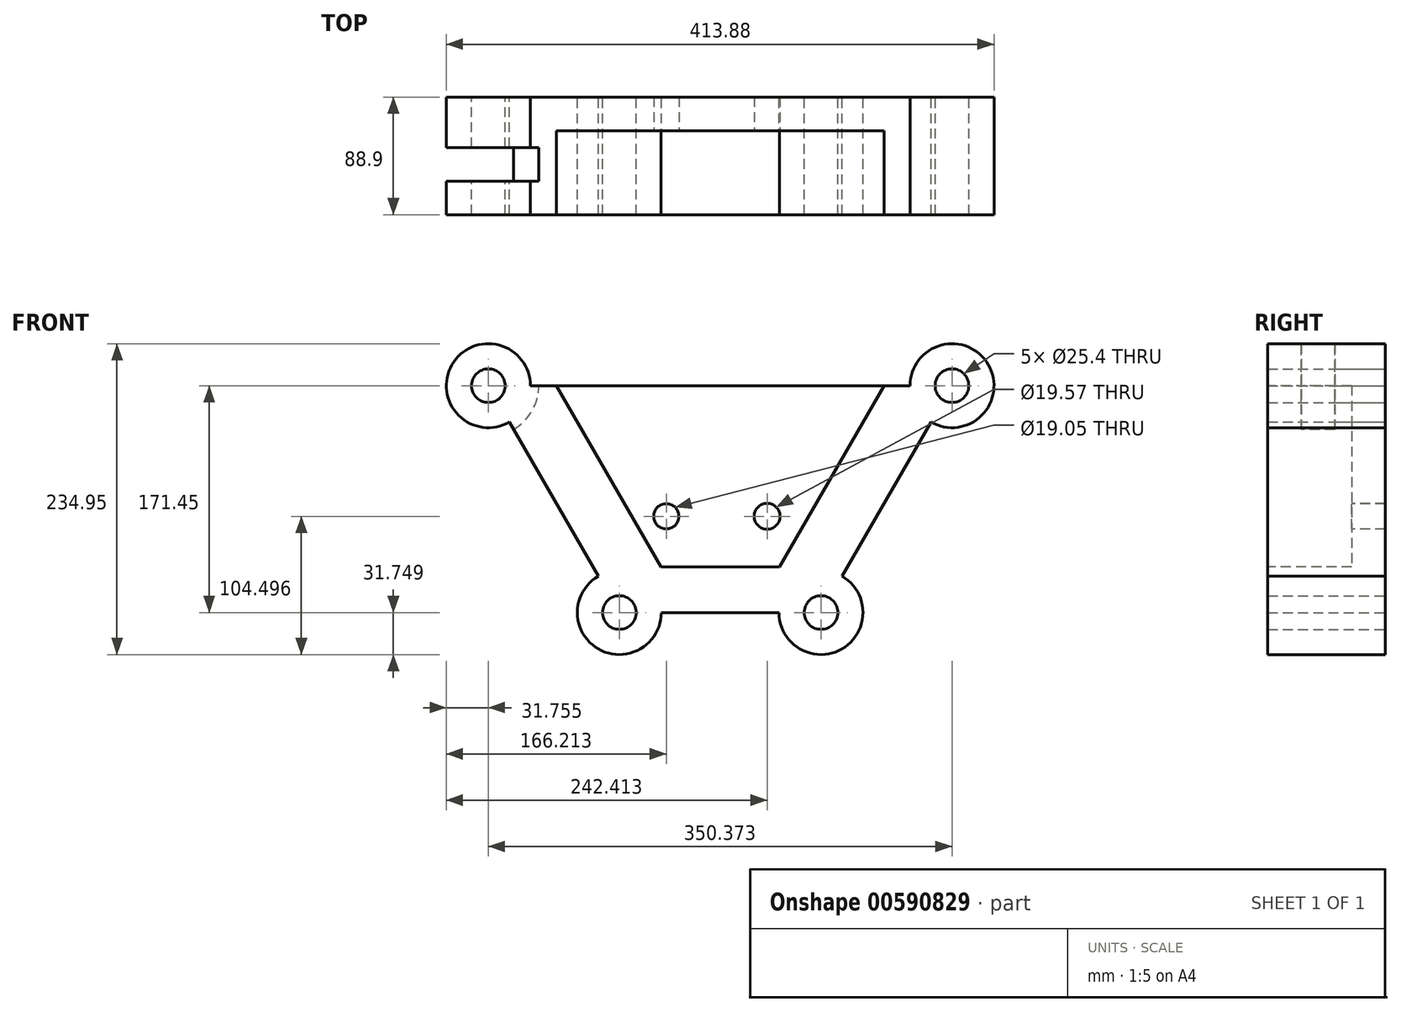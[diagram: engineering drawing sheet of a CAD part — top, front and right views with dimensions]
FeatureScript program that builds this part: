
annotation { "Feature Type Name" : "Feature", "Feature Type Description" : "" }
export const myFeature = defineFeature(function(context is Context, id is Id, definition is map)
    precondition{}
    {
        {
            var Q0;
            Q0=qCreatedBy(makeId("Front.planeOp"),FACE);
            var sketch = newSketch(context, id + "F0", { "sketchPlane" : qUnion([Q0])});
            skLineSegment(sketch, "E0", {"start": v(-63.64, -75.33) * mm, "end": v(88.76, -75.33) * mm});
            skLineSegment(sketch, "E1", {"start": v(-63.64, -75.33) * mm, "end": v(-162.63, 96.12) * mm});
            skLineSegment(sketch, "E2", {"start": v(-162.63, 96.12) * mm, "end": v(187.75, 96.12) * mm});
            skLineSegment(sketch, "E3", {"start": v(187.75, 96.12) * mm, "end": v(88.76, -75.33) * mm});
            skCircle(sketch, "E4", {"center": v(-63.64, -75.33) * mm, "radius": 12.7 * mm});
            skCircle(sketch, "E5", {"center": v(88.76, -75.33) * mm, "radius": 12.7 * mm});
            skCircle(sketch, "E6", {"center": v(-162.63, 96.12) * mm, "radius": 12.7 * mm});
            skCircle(sketch, "E7", {"center": v(187.75, 96.12) * mm, "radius": 12.7 * mm});
            skCircle(sketch, "E8", {"center": v(187.75, 96.12) * mm, "radius": 31.75 * mm});
            skCircle(sketch, "E9", {"center": v(88.76, -75.33) * mm, "radius": 31.75 * mm});
            skCircle(sketch, "E10", {"center": v(-63.64, -75.33) * mm, "radius": 31.75 * mm});
            skCircle(sketch, "E11", {"center": v(-162.63, 96.12) * mm, "radius": 31.75 * mm});
            skSolve(sketch);
        }
        {
            var Q0;
            {var subQ0=sQuery(id+"F0.wireOp",EDGE,"E11");var subQ1=sQuery(id+"F0.wireOp",EDGE,"E1");var subQ2=makeQuery(id+"F0.imprint","INTERSECT",VERTEX,{"derivedFrom":[subQ1,subQ0]});Q0=makeQuery(id+"F0.imprint","IMPRINT",FACE,{"disambiguationData":[TD([[makeQuery(id+"F0.imprint","IMPRINT",EDGE,{"disambiguationData":[TD([[subQ2,-1.0]])],"derivedFrom":subQ1}),1.0]])]});}
            var Q1;
            {var subQ0=sQuery(id+"F0.wireOp",EDGE,"E11");var subQ1=sQuery(id+"F0.wireOp",EDGE,"E1");var subQ2=makeQuery(id+"F0.imprint","INTERSECT",VERTEX,{"derivedFrom":[subQ1,subQ0]});Q1=makeQuery(id+"F0.imprint","IMPRINT",FACE,{"disambiguationData":[TD([[makeQuery(id+"F0.imprint","IMPRINT",EDGE,{"disambiguationData":[TD([[subQ2,-1.0]])],"derivedFrom":subQ1}),-1.0]])]});}
            var Q2;
            {var subQ0=sQuery(id+"F0.wireOp",EDGE,"E8");var subQ1=sQuery(id+"F0.wireOp",EDGE,"E2");var subQ2=makeQuery(id+"F0.imprint","INTERSECT",VERTEX,{"derivedFrom":[subQ1,subQ0]});Q2=makeQuery(id+"F0.imprint","IMPRINT",FACE,{"disambiguationData":[TD([[makeQuery(id+"F0.imprint","IMPRINT",EDGE,{"disambiguationData":[TD([[subQ2,-1.0]])],"derivedFrom":subQ1}),1.0]])]});}
            var Q3;
            {var subQ9=sQuery(id+"F0.wireOp",EDGE,"E10");var subQ13=sQuery(id+"F0.wireOp",EDGE,"E0");var subQ14=makeQuery(id+"F0.imprint","INTERSECT",VERTEX,{"derivedFrom":[subQ13,subQ9]});Q3=makeQuery(id+"F0.imprint","IMPRINT",FACE,{"disambiguationData":[TD([[makeQuery(id+"F0.imprint","IMPRINT",EDGE,{"disambiguationData":[TD([[subQ14,-1.0]])],"derivedFrom":subQ13}),1.0]])]});}
            var Q4;
            {var subQ0=sQuery(id+"F0.wireOp",EDGE,"E9");var subQ1=sQuery(id+"F0.wireOp",EDGE,"E0");var subQ2=makeQuery(id+"F0.imprint","INTERSECT",VERTEX,{"derivedFrom":[subQ1,subQ0]});Q4=makeQuery(id+"F0.imprint","IMPRINT",FACE,{"disambiguationData":[TD([[makeQuery(id+"F0.imprint","IMPRINT",EDGE,{"disambiguationData":[TD([[subQ2,-1.0]])],"derivedFrom":subQ1}),-1.0]])]});}
            var Q5;
            {var subQ0=sQuery(id+"F0.wireOp",EDGE,"E9");var subQ1=sQuery(id+"F0.wireOp",EDGE,"E0");var subQ2=makeQuery(id+"F0.imprint","INTERSECT",VERTEX,{"derivedFrom":[subQ1,subQ0]});Q5=makeQuery(id+"F0.imprint","IMPRINT",FACE,{"disambiguationData":[TD([[makeQuery(id+"F0.imprint","IMPRINT",EDGE,{"disambiguationData":[TD([[subQ2,-1.0]])],"derivedFrom":subQ1}),1.0]])]});}
            var Q6;
            {var subQ0=sQuery(id+"F0.wireOp",EDGE,"E10");var subQ1=sQuery(id+"F0.wireOp",EDGE,"E0");var subQ2=makeQuery(id+"F0.imprint","INTERSECT",VERTEX,{"derivedFrom":[subQ1,subQ0]});Q6=makeQuery(id+"F0.imprint","IMPRINT",FACE,{"disambiguationData":[TD([[makeQuery(id+"F0.imprint","IMPRINT",EDGE,{"disambiguationData":[TD([[subQ2,1.0]])],"derivedFrom":subQ1}),-1.0]])]});}
            var Q7;
            {var subQ0=sQuery(id+"F0.wireOp",EDGE,"E10");var subQ1=sQuery(id+"F0.wireOp",EDGE,"E0");var subQ2=makeQuery(id+"F0.imprint","INTERSECT",VERTEX,{"derivedFrom":[subQ1,subQ0]});Q7=makeQuery(id+"F0.imprint","IMPRINT",FACE,{"disambiguationData":[TD([[makeQuery(id+"F0.imprint","IMPRINT",EDGE,{"disambiguationData":[TD([[subQ2,1.0]])],"derivedFrom":subQ1}),1.0]])]});}
            var Q8;
            {var subQ0=sQuery(id+"F0.wireOp",EDGE,"E8");var subQ1=sQuery(id+"F0.wireOp",EDGE,"E2");var subQ2=makeQuery(id+"F0.imprint","INTERSECT",VERTEX,{"derivedFrom":[subQ1,subQ0]});Q8=makeQuery(id+"F0.imprint","IMPRINT",FACE,{"disambiguationData":[TD([[makeQuery(id+"F0.imprint","IMPRINT",EDGE,{"disambiguationData":[TD([[subQ2,-1.0]])],"derivedFrom":subQ1}),-1.0]])]});}
            extrude(context, id + "F1", {"entities" : qUnion([Q0, Q1, Q2, Q3, Q4, Q5, Q6, Q7, Q8]), "endBound" : BoundingType.SYMMETRIC, "depth" : 101.6 * mm, "offsetDistance" : 25.4 * mm});
        }
        {
            var Q0;
            Q0=makeQuery(id+"F1.opExtrude","CAP_FACE",FACE,{"disambiguationData":[OSD([sQuery(id+"F0.wireOp",EDGE,"E0"),sQuery(id+"F0.wireOp",EDGE,"E1"),sQuery(id+"F0.wireOp",EDGE,"E2"),sQuery(id+"F0.wireOp",EDGE,"E3"),sQuery(id+"F0.wireOp",EDGE,"E4"),sQuery(id+"F0.wireOp",EDGE,"E5"),sQuery(id+"F0.wireOp",EDGE,"E6"),sQuery(id+"F0.wireOp",EDGE,"E7"),sQuery(id+"F0.wireOp",EDGE,"E8"),sQuery(id+"F0.wireOp",EDGE,"E9"),sQuery(id+"F0.wireOp",EDGE,"E10"),sQuery(id+"F0.wireOp",EDGE,"E11")])],"isStart":false});
            var sketch = newSketch(context, id + "F2", { "sketchPlane" : qUnion([Q0])});
            skLineSegment(sketch, "E12", {"start": v(-111.3, 96.12) * mm, "end": v(-32.32, -40.68) * mm});
            skLineSegment(sketch, "E13", {"start": v(-32.32, -40.68) * mm, "end": v(57.44, -40.68) * mm});
            skLineSegment(sketch, "E14", {"start": v(57.44, -40.68) * mm, "end": v(136.42, 96.12) * mm});
            skLineSegment(sketch, "E15", {"start": v(136.42, 96.12) * mm, "end": v(-111.3, 96.12) * mm});
            skSolve(sketch);
        }
        {
            var Q0;
            Q0=makeQuery(id+"F2.imprint","IMPRINT",FACE,{"disambiguationData":[TD([[makeQuery(id+"F2.imprint","IMPRINT",EDGE,{"derivedFrom":sQuery(id+"F2.wireOp",EDGE,"E12")}),1.0]])]});
            extrude(context, id + "F3", {"entities" : qUnion([Q0]), "operationType" : NewBodyOperationType.REMOVE, "oppositeDirection" : true, "depth" : 76.2 * mm, "offsetDistance" : 25.4 * mm});
        }
        {
            var Q0;
            Q0=qCreatedBy(makeId("Front.planeOp"),FACE);
            var sketch = newSketch(context, id + "F4", { "sketchPlane" : qUnion([Q0])});
            skCircle(sketch, "E16", {"center": v(-162.63, 96.12) * mm, "radius": 38.1 * mm});
            skCircle(sketch, "E17", {"center": v(187.75, 96.12) * mm, "radius": 38.1 * mm});
            skCircle(sketch, "E18", {"center": v(-63.64, -75.33) * mm, "radius": 38.1 * mm});
            skCircle(sketch, "E19", {"center": v(88.76, -75.33) * mm, "radius": 38.1 * mm});
            skSolve(sketch);
        }
        {
            var Q0;
            Q0=makeQuery(id+"F4.imprint","IMPRINT",FACE,{"disambiguationData":[TD([[makeQuery(id+"F4.imprint","IMPRINT",EDGE,{"derivedFrom":sQuery(id+"F4.wireOp",EDGE,"E16")}),1.0]])]});
            var Q1;
            Q1=makeQuery(id+"F1.opExtrude","CAP_FACE",FACE,{"disambiguationData":[OSD([sQuery(id+"F0.wireOp",EDGE,"E0"),sQuery(id+"F0.wireOp",EDGE,"E1"),sQuery(id+"F0.wireOp",EDGE,"E2"),sQuery(id+"F0.wireOp",EDGE,"E3"),sQuery(id+"F0.wireOp",EDGE,"E4"),sQuery(id+"F0.wireOp",EDGE,"E5"),sQuery(id+"F0.wireOp",EDGE,"E6"),sQuery(id+"F0.wireOp",EDGE,"E7"),sQuery(id+"F0.wireOp",EDGE,"E8"),sQuery(id+"F0.wireOp",EDGE,"E9"),sQuery(id+"F0.wireOp",EDGE,"E10"),sQuery(id+"F0.wireOp",EDGE,"E11")])],"isStart":false});
            extrude(context, id + "F5", {"entities" : qUnion([Q0, Q1]), "operationType" : NewBodyOperationType.REMOVE, "endBound" : BoundingType.SYMMETRIC, "oppositeDirection" : true, "depth" : 25.4 * mm, "offsetDistance" : 25.4 * mm});
        }
        {
            var Q0;
            Q0=makeQuery(id+"F3.boolean.opBoolean","COPY",FACE,{"derivedFrom":makeQuery(id+"F3.opExtrude","CAP_FACE",FACE,{"disambiguationData":[OSD([sQuery(id+"F2.wireOp",EDGE,"E12"),sQuery(id+"F2.wireOp",EDGE,"E13"),sQuery(id+"F2.wireOp",EDGE,"E14"),sQuery(id+"F2.wireOp",EDGE,"E15")])],"isStart":false})});
            var sketch = newSketch(context, id + "F6", { "sketchPlane" : qUnion([Q0])});
            skCircle(sketch, "E20", {"center": v(-28.17, -2.58) * mm, "radius": 9.53 * mm});
            skCircle(sketch, "E21", {"center": v(48.03, -2.58) * mm, "radius": 9.78 * mm});
            skLineSegment(sketch, "E22", {"start": v(-28.17, -2.58) * mm, "end": v(48.03, -2.58) * mm, "construction": true});
            skPoint(sketch, "E23", {"position": v(9.93, 0) * mm});
            skLineSegment(sketch, "E24", {"start": v(9.93, 0) * mm, "end": v(9.93, -40.68) * mm, "construction": true});
            skPoint(sketch, "E24.endSnap0", {"position": v(12.56, -40.68) * mm});
            skLineSegment(sketch, "E25", {"start": v(9.93, -40.68) * mm, "end": v(12.56, -40.68) * mm, "construction": true});
            skSolve(sketch);
        }
        {
            var Q0;
            Q0=makeQuery(id+"F6.imprint","IMPRINT",FACE,{"disambiguationData":[TD([[makeQuery(id+"F6.imprint","IMPRINT",EDGE,{"derivedFrom":sQuery(id+"F6.wireOp",EDGE,"E20")}),1.0]])]});
            var Q1;
            Q1=makeQuery(id+"F6.imprint","IMPRINT",FACE,{"disambiguationData":[TD([[makeQuery(id+"F6.imprint","IMPRINT",EDGE,{"derivedFrom":sQuery(id+"F6.wireOp",EDGE,"E21")}),1.0]])]});
            extrude(context, id + "F7", {"entities" : qUnion([Q0, Q1]), "operationType" : NewBodyOperationType.REMOVE, "endBound" : BoundingType.THROUGH_ALL, "oppositeDirection" : true, "depth" : 25.4 * mm, "offsetDistance" : 25.4 * mm});
        }
    });
